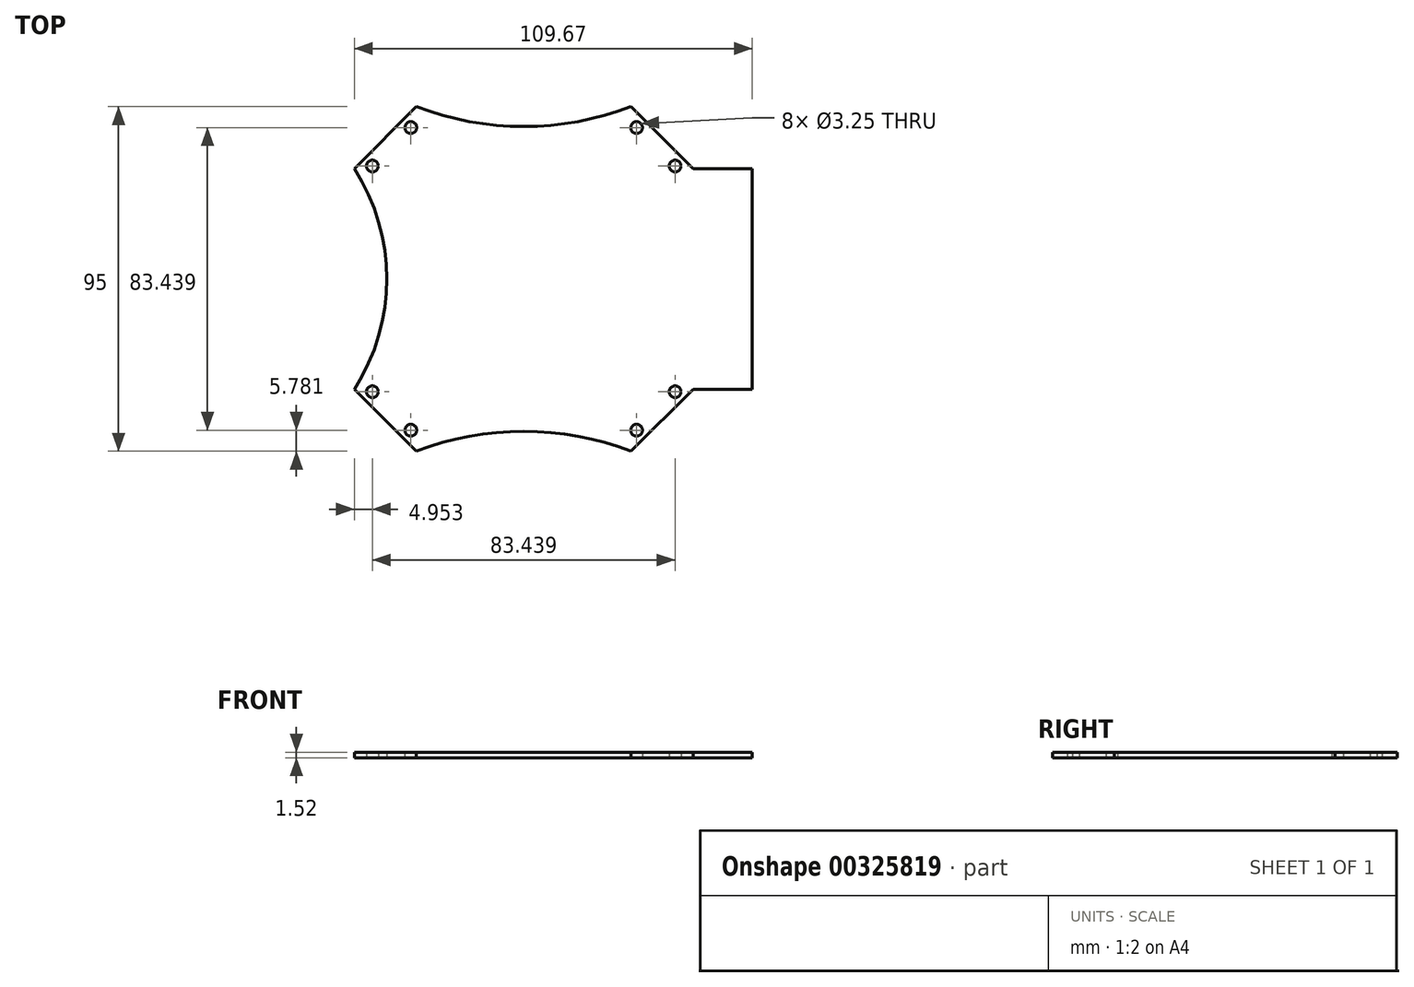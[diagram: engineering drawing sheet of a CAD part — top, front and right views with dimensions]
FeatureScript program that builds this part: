
annotation { "Feature Type Name" : "Feature", "Feature Type Description" : "" }
export const myFeature = defineFeature(function(context is Context, id is Id, definition is map)
    precondition{}
    {
        {
            var Q0;
            Q0=qCreatedBy(makeId("Top.planeOp"),FACE);
            var sketch = newSketch(context, id + "F0", { "sketchPlane" : qUnion([Q0])});
            skLineSegment(sketch, "E0", {"start": v(31.11, -41.72) * mm, "end": v(18.33, -41.72) * mm, "construction": true});
            skLineSegment(sketch, "E1", {"start": v(31.11, -41.72) * mm, "end": v(31.11, 56.02) * mm, "construction": true});
            skLineSegment(sketch, "E2", {"start": v(31.11, -41.72) * mm, "end": v(-24, 13.4) * mm, "construction": true});
            skLineSegment(sketch, "E3", {"start": v(-13.96, -13.96) * mm, "end": v(43.52, 43.52) * mm, "construction": true});
            skCircle(sketch, "E4", {"center": v(-10.6, -10.6) * mm, "radius": 1.63 * mm});
            skCircle(sketch, "E5", {"center": v(0, 0) * mm, "radius": 1.63 * mm});
            skLineSegment(sketch, "E6", {"start": v(-15.56, -11.31) * mm, "end": v(1.54, 5.78) * mm});
            skLineSegment(sketch, "E7.MirrorCS", {"start": v(77.78, -11.31) * mm, "end": v(60.69, 5.78) * mm});
            skCircle(sketch, "E8.MirrorC", {"center": v(62.23, 0) * mm, "radius": 1.63 * mm});
            skCircle(sketch, "E9.MirrorC", {"center": v(72.83, -10.6) * mm, "radius": 1.63 * mm});
            skLineSegment(sketch, "E10.MirrorCS", {"start": v(-15.56, -72.12) * mm, "end": v(1.54, -89.22) * mm});
            skLineSegment(sketch, "E11.MirrorCS", {"start": v(77.78, -72.12) * mm, "end": v(60.69, -89.22) * mm});
            skCircle(sketch, "E12.MirrorC", {"center": v(72.83, -72.83) * mm, "radius": 1.63 * mm});
            skCircle(sketch, "E13.MirrorC", {"center": v(62.23, -83.44) * mm, "radius": 1.63 * mm});
            skCircle(sketch, "E14.MirrorC", {"center": v(0, -83.44) * mm, "radius": 1.63 * mm});
            skCircle(sketch, "E15.MirrorC", {"center": v(-10.6, -72.83) * mm, "radius": 1.63 * mm});
            skArc(sketch, "E16", {"start": v(-15.56, -72.12) * mm, "mid": v(-6.64, -41.72) * mm, "end": v(-15.56, -11.31) * mm});
            skPoint(sketch, "E17.orphan", {"position": v(7.57, 76.41) * mm});
            skArc(sketch, "E18", {"start": v(60.69, -89.22) * mm, "mid": v(31.11, -83.72) * mm, "end": v(1.54, -89.22) * mm});
            skArc(sketch, "E19.MirrorCS", {"start": v(60.69, 5.78) * mm, "mid": v(31.11, 0.28) * mm, "end": v(1.54, 5.78) * mm});
            skPoint(sketch, "E20", {"position": v(-5.3, -5.3) * mm});
            skLineSegment(sketch, "E21", {"start": v(77.78, -11.31) * mm, "end": v(94.11, -11.31) * mm});
            skLineSegment(sketch, "E22", {"start": v(94.11, -11.31) * mm, "end": v(94.11, -72.12) * mm});
            skLineSegment(sketch, "E23", {"start": v(94.11, -72.12) * mm, "end": v(77.78, -72.12) * mm});
            skSolve(sketch);
        }
        {
            var Q0;
            Q0=makeQuery(id+"F0.imprint","IMPRINT",FACE,{"disambiguationData":[TD([[makeQuery(id+"F0.imprint","IMPRINT",EDGE,{"derivedFrom":sQuery(id+"F0.wireOp",EDGE,"E4")}),-1.0]])]});
            extrude(context, id + "F1", {"entities" : qUnion([Q0]), "depth" : 1.52 * mm, "offsetDistance" : 25 * mm});
        }
    });
